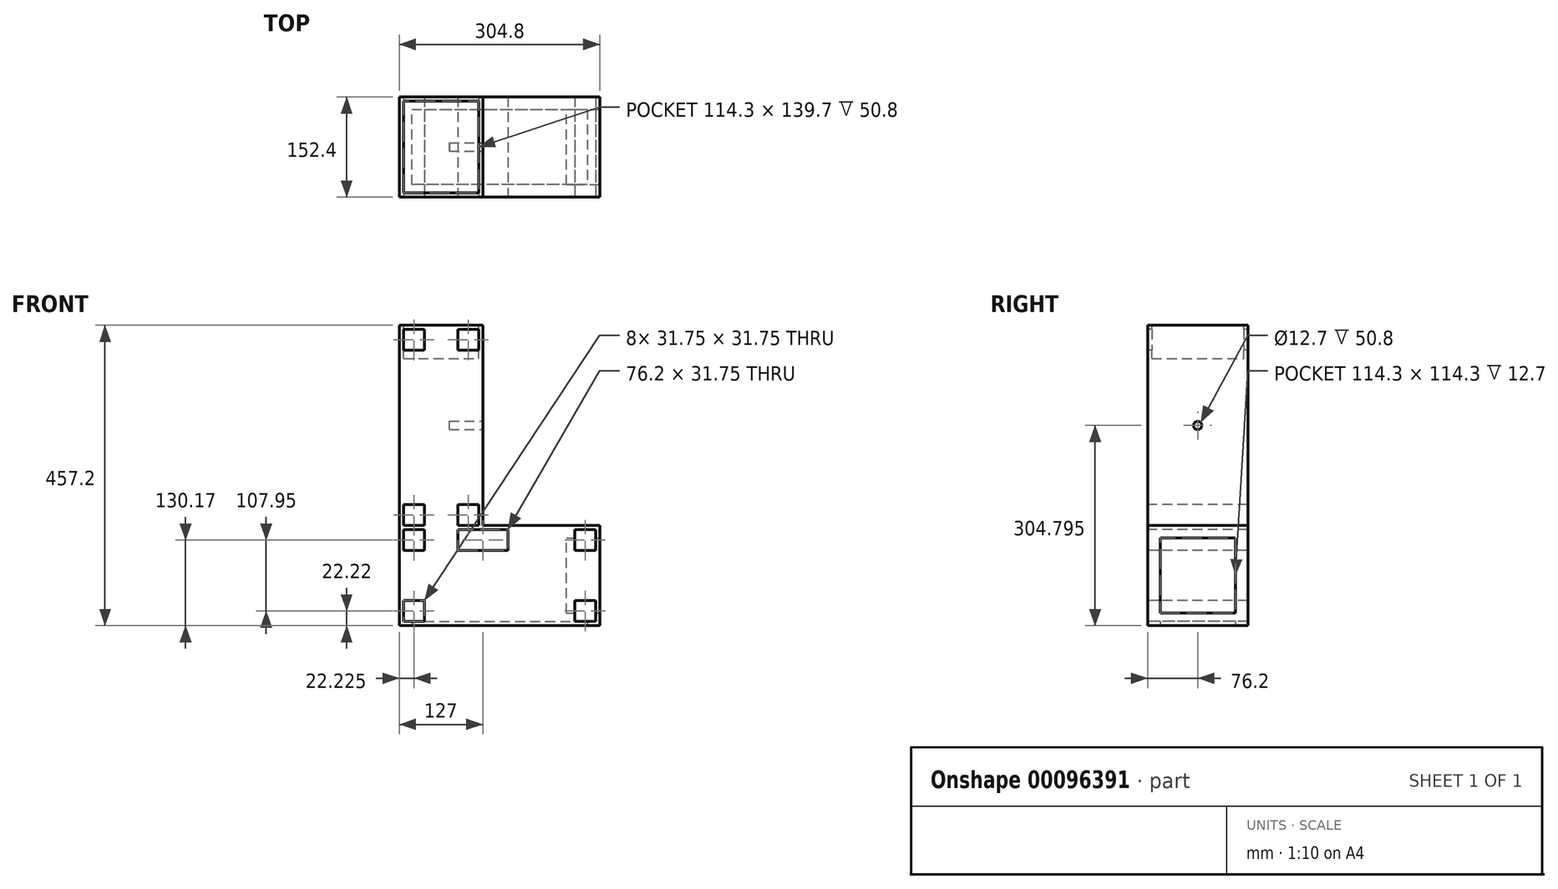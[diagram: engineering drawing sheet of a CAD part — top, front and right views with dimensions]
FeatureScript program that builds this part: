
annotation { "Feature Type Name" : "Feature", "Feature Type Description" : "" }
export const myFeature = defineFeature(function(context is Context, id is Id, definition is map)
    precondition{}
    {
        {
            var Q0;
            Q0=qCreatedBy(makeId("Front.planeOp"),FACE);
            var sketch = newSketch(context, id + "F0", { "sketchPlane" : qUnion([Q0])});
            skLineSegment(sketch, "E0", {"start": v(-127, -226.18) * mm, "end": v(177.8, -226.18) * mm});
            skLineSegment(sketch, "E1", {"start": v(177.8, -226.18) * mm, "end": v(177.8, -73.78) * mm});
            skLineSegment(sketch, "E2", {"start": v(177.8, -73.78) * mm, "end": v(0, -73.78) * mm});
            skLineSegment(sketch, "E3", {"start": v(-127, -226.18) * mm, "end": v(-127, 231.02) * mm});
            skLineSegment(sketch, "E4", {"start": v(-127, 231.02) * mm, "end": v(0, 231.02) * mm});
            skLineSegment(sketch, "E5", {"start": v(0, 231.02) * mm, "end": v(0, -73.78) * mm});
            skLineSegment(sketch, "E6", {"start": v(177.8, -226.18) * mm, "end": v(177.8, -188.08) * mm});
            skLineSegment(sketch, "E7", {"start": v(177.8, -188.08) * mm, "end": v(139.7, -188.08) * mm});
            skLineSegment(sketch, "E8", {"start": v(139.7, -188.08) * mm, "end": v(139.7, -226.18) * mm});
            skLineSegment(sketch, "E9", {"start": v(-127, -226.18) * mm, "end": v(-88.9, -226.18) * mm});
            skLineSegment(sketch, "E10", {"start": v(-88.9, -226.18) * mm, "end": v(-88.9, -188.08) * mm});
            skLineSegment(sketch, "E11", {"start": v(-88.9, -188.08) * mm, "end": v(-127, -188.08) * mm});
            skLineSegment(sketch, "E12", {"start": v(-127, 231.02) * mm, "end": v(-127, 192.92) * mm});
            skLineSegment(sketch, "E13", {"start": v(-127, 192.92) * mm, "end": v(-88.9, 192.92) * mm});
            skLineSegment(sketch, "E14", {"start": v(-88.9, 192.92) * mm, "end": v(-88.9, 231.02) * mm});
            skLineSegment(sketch, "E15", {"start": v(-38.1, 231.02) * mm, "end": v(-38.1, 192.92) * mm});
            skLineSegment(sketch, "E16", {"start": v(-38.1, 192.92) * mm, "end": v(0, 192.92) * mm});
            skLineSegment(sketch, "E17", {"start": v(0, -35.68) * mm, "end": v(-38.1, -35.68) * mm});
            skLineSegment(sketch, "E18", {"start": v(-38.1, -35.68) * mm, "end": v(-38.1, -111.88) * mm});
            skLineSegment(sketch, "E19", {"start": v(-38.1, -111.88) * mm, "end": v(38.1, -111.88) * mm});
            skLineSegment(sketch, "E20", {"start": v(38.1, -111.88) * mm, "end": v(38.1, -73.78) * mm});
            skLineSegment(sketch, "E21", {"start": v(139.7, -73.78) * mm, "end": v(139.7, -111.88) * mm});
            skLineSegment(sketch, "E22", {"start": v(139.7, -111.88) * mm, "end": v(177.8, -111.88) * mm});
            skLineSegment(sketch, "E23", {"start": v(-120.65, 192.92) * mm, "end": v(-120.65, 231.02) * mm});
            skLineSegment(sketch, "E24", {"start": v(-127, 224.67) * mm, "end": v(-88.9, 224.67) * mm});
            skLineSegment(sketch, "E25", {"start": v(0, 224.67) * mm, "end": v(-38.1, 224.67) * mm});
            skLineSegment(sketch, "E26", {"start": v(-6.35, 231.02) * mm, "end": v(-6.35, 192.92) * mm});
            skLineSegment(sketch, "E27", {"start": v(-6.35, -35.68) * mm, "end": v(-6.35, -80.13) * mm});
            skLineSegment(sketch, "E28", {"start": v(-6.35, -80.13) * mm, "end": v(38.1, -80.13) * mm});
            skLineSegment(sketch, "E29", {"start": v(139.7, -80.13) * mm, "end": v(177.8, -80.13) * mm});
            skLineSegment(sketch, "E30", {"start": v(171.45, -73.78) * mm, "end": v(171.45, -111.88) * mm});
            skLineSegment(sketch, "E31", {"start": v(171.45, -188.08) * mm, "end": v(171.45, -226.18) * mm});
            skLineSegment(sketch, "E32", {"start": v(-120.65, -188.08) * mm, "end": v(-120.65, -226.18) * mm});
            skLineSegment(sketch, "E33", {"start": v(-127, -219.83) * mm, "end": v(-88.9, -219.83) * mm});
            skLineSegment(sketch, "E34", {"start": v(139.7, -219.83) * mm, "end": v(177.8, -219.83) * mm});
            skSolve(sketch);
        }
        {
            var Q0;
            {var subQ27=sQuery(id+"F0.wireOp",EDGE,"E18");Q0=makeQuery(id+"F0.imprint","IMPRINT",FACE,{"disambiguationData":[TD([[makeQuery(id+"F0.imprint","IMPRINT",EDGE,{"derivedFrom":subQ27}),-1.0]])]});}
            var Q1;
            {var subQ0=sQuery(id+"F0.wireOp",EDGE,"E16");var subQ1=sQuery(id+"F0.wireOp",EDGE,"E5");var subQ2=makeQuery(id+"F0.imprint","INTERSECT",VERTEX,{"derivedFrom":[subQ1,subQ0]});Q1=makeQuery(id+"F0.imprint","IMPRINT",FACE,{"disambiguationData":[TD([[makeQuery(id+"F0.imprint","IMPRINT",EDGE,{"disambiguationData":[TD([[subQ2,1.0]])],"derivedFrom":subQ1}),-1.0]])]});}
            var Q2;
            {var subQ0=sQuery(id+"F0.wireOp",EDGE,"E15");var subQ1=sQuery(id+"F0.wireOp",EDGE,"E4");var subQ2=makeQuery(id+"F0.imprint","INTERSECT",VERTEX,{"derivedFrom":[subQ1,subQ0]});Q2=makeQuery(id+"F0.imprint","IMPRINT",FACE,{"disambiguationData":[TD([[makeQuery(id+"F0.imprint","IMPRINT",EDGE,{"disambiguationData":[TD([[subQ2,-1.0]])],"derivedFrom":subQ1}),-1.0]])]});}
            var Q3;
            {var subQ0=sQuery(id+"F0.wireOp",EDGE,"E16");var subQ1=sQuery(id+"F0.wireOp",EDGE,"E15");var subQ2=makeQuery(id+"F0.imprint","INTERSECT",VERTEX,{"derivedFrom":[subQ1,subQ0]});Q3=makeQuery(id+"F0.imprint","IMPRINT",FACE,{"disambiguationData":[TD([[makeQuery(id+"F0.imprint","IMPRINT",EDGE,{"disambiguationData":[TD([[subQ2,1.0]])],"derivedFrom":subQ1}),1.0]])]});}
            var Q4;
            {var subQ0=sQuery(id+"F0.wireOp",EDGE,"E5");var subQ1=sQuery(id+"F0.wireOp",EDGE,"E4");var subQ2=makeQuery(id+"F0.imprint","INTERSECT",VERTEX,{"derivedFrom":[subQ1,subQ0]});Q4=makeQuery(id+"F0.imprint","IMPRINT",FACE,{"disambiguationData":[TD([[makeQuery(id+"F0.imprint","IMPRINT",EDGE,{"disambiguationData":[TD([[subQ2,1.0]])],"derivedFrom":subQ1}),-1.0]])]});}
            var Q5;
            {var subQ0=sQuery(id+"F0.wireOp",EDGE,"E12");var subQ1=sQuery(id+"F0.wireOp",EDGE,"E4");var subQ2=makeQuery(id+"F0.imprint","INTERSECT",VERTEX,{"derivedFrom":[subQ1,subQ0]});Q5=makeQuery(id+"F0.imprint","IMPRINT",FACE,{"disambiguationData":[TD([[makeQuery(id+"F0.imprint","IMPRINT",EDGE,{"disambiguationData":[TD([[subQ2,-1.0]])],"derivedFrom":subQ1}),-1.0]])]});}
            var Q6;
            {var subQ0=sQuery(id+"F0.wireOp",EDGE,"E14");var subQ1=sQuery(id+"F0.wireOp",EDGE,"E4");var subQ2=makeQuery(id+"F0.imprint","INTERSECT",VERTEX,{"derivedFrom":[subQ1,subQ0]});Q6=makeQuery(id+"F0.imprint","IMPRINT",FACE,{"disambiguationData":[TD([[makeQuery(id+"F0.imprint","IMPRINT",EDGE,{"disambiguationData":[TD([[subQ2,1.0]])],"derivedFrom":subQ1}),-1.0]])]});}
            var Q7;
            {var subQ0=sQuery(id+"F0.wireOp",EDGE,"E14");var subQ1=sQuery(id+"F0.wireOp",EDGE,"E13");var subQ2=makeQuery(id+"F0.imprint","INTERSECT",VERTEX,{"derivedFrom":[subQ1,subQ0]});Q7=makeQuery(id+"F0.imprint","IMPRINT",FACE,{"disambiguationData":[TD([[makeQuery(id+"F0.imprint","IMPRINT",EDGE,{"disambiguationData":[TD([[subQ2,1.0]])],"derivedFrom":subQ1}),1.0]])]});}
            var Q8;
            {var subQ0=sQuery(id+"F0.wireOp",EDGE,"E13");var subQ5=sQuery(id+"F0.wireOp",EDGE,"E23");var subQ6=makeQuery(id+"F0.imprint","INTERSECT",VERTEX,{"derivedFrom":[subQ0,subQ5]});Q8=makeQuery(id+"F0.imprint","IMPRINT",FACE,{"disambiguationData":[TD([[makeQuery(id+"F0.imprint","IMPRINT",EDGE,{"disambiguationData":[TD([[subQ6,-1.0]])],"derivedFrom":subQ5}),1.0]])]});}
            var Q9;
            {var subQ3=sQuery(id+"F0.wireOp",EDGE,"E27");Q9=makeQuery(id+"F0.imprint","IMPRINT",FACE,{"disambiguationData":[TD([[makeQuery(id+"F0.imprint","IMPRINT",EDGE,{"derivedFrom":subQ3}),1.0]])]});}
            var Q10;
            {var subQ4=sQuery(id+"F0.wireOp",EDGE,"E18");Q10=makeQuery(id+"F0.imprint","IMPRINT",FACE,{"disambiguationData":[TD([[makeQuery(id+"F0.imprint","IMPRINT",EDGE,{"derivedFrom":subQ4}),1.0]])]});}
            var Q11;
            {var subQ0=sQuery(id+"F0.wireOp",EDGE,"E22");var subQ1=sQuery(id+"F0.wireOp",EDGE,"E21");var subQ2=makeQuery(id+"F0.imprint","INTERSECT",VERTEX,{"derivedFrom":[subQ1,subQ0]});Q11=makeQuery(id+"F0.imprint","IMPRINT",FACE,{"disambiguationData":[TD([[makeQuery(id+"F0.imprint","IMPRINT",EDGE,{"disambiguationData":[TD([[subQ2,1.0]])],"derivedFrom":subQ1}),1.0]])]});}
            var Q12;
            {var subQ0=sQuery(id+"F0.wireOp",EDGE,"E21");var subQ1=sQuery(id+"F0.wireOp",EDGE,"E2");var subQ2=makeQuery(id+"F0.imprint","INTERSECT",VERTEX,{"derivedFrom":[subQ1,subQ0]});Q12=makeQuery(id+"F0.imprint","IMPRINT",FACE,{"disambiguationData":[TD([[makeQuery(id+"F0.imprint","IMPRINT",EDGE,{"disambiguationData":[TD([[subQ2,1.0]])],"derivedFrom":subQ1}),1.0]])]});}
            var Q13;
            {var subQ0=sQuery(id+"F0.wireOp",EDGE,"E2");var subQ1=sQuery(id+"F0.wireOp",EDGE,"E1");var subQ2=makeQuery(id+"F0.imprint","INTERSECT",VERTEX,{"derivedFrom":[subQ1,subQ0]});Q13=makeQuery(id+"F0.imprint","IMPRINT",FACE,{"disambiguationData":[TD([[makeQuery(id+"F0.imprint","IMPRINT",EDGE,{"disambiguationData":[TD([[subQ2,1.0]])],"derivedFrom":subQ1}),1.0]])]});}
            var Q14;
            {var subQ0=sQuery(id+"F0.wireOp",EDGE,"E22");var subQ1=sQuery(id+"F0.wireOp",EDGE,"E1");var subQ2=makeQuery(id+"F0.imprint","INTERSECT",VERTEX,{"derivedFrom":[subQ1,subQ0]});Q14=makeQuery(id+"F0.imprint","IMPRINT",FACE,{"disambiguationData":[TD([[makeQuery(id+"F0.imprint","IMPRINT",EDGE,{"disambiguationData":[TD([[subQ2,-1.0]])],"derivedFrom":subQ1}),1.0]])]});}
            var Q15;
            {var subQ0=sQuery(id+"F0.wireOp",EDGE,"E6");var subQ1=sQuery(id+"F0.wireOp",EDGE,"E0");var subQ2=makeQuery(id+"F0.imprint","INTERSECT",VERTEX,{"derivedFrom":[subQ1,subQ0]});Q15=makeQuery(id+"F0.imprint","IMPRINT",FACE,{"disambiguationData":[TD([[makeQuery(id+"F0.imprint","IMPRINT",EDGE,{"disambiguationData":[TD([[subQ2,1.0]])],"derivedFrom":subQ1}),1.0]])]});}
            var Q16;
            {var subQ0=sQuery(id+"F0.wireOp",EDGE,"E8");var subQ1=sQuery(id+"F0.wireOp",EDGE,"E0");var subQ2=makeQuery(id+"F0.imprint","INTERSECT",VERTEX,{"derivedFrom":[subQ1,subQ0]});Q16=makeQuery(id+"F0.imprint","IMPRINT",FACE,{"disambiguationData":[TD([[makeQuery(id+"F0.imprint","IMPRINT",EDGE,{"disambiguationData":[TD([[subQ2,-1.0]])],"derivedFrom":subQ1}),1.0]])]});}
            var Q17;
            {var subQ0=sQuery(id+"F0.wireOp",EDGE,"E8");var subQ1=sQuery(id+"F0.wireOp",EDGE,"E7");var subQ2=makeQuery(id+"F0.imprint","INTERSECT",VERTEX,{"derivedFrom":[subQ1,subQ0]});Q17=makeQuery(id+"F0.imprint","IMPRINT",FACE,{"disambiguationData":[TD([[makeQuery(id+"F0.imprint","IMPRINT",EDGE,{"disambiguationData":[TD([[subQ2,1.0]])],"derivedFrom":subQ1}),1.0]])]});}
            var Q18;
            {var subQ0=sQuery(id+"F0.wireOp",EDGE,"E7");var subQ5=sQuery(id+"F0.wireOp",EDGE,"E31");var subQ6=makeQuery(id+"F0.imprint","INTERSECT",VERTEX,{"derivedFrom":[subQ0,subQ5]});Q18=makeQuery(id+"F0.imprint","IMPRINT",FACE,{"disambiguationData":[TD([[makeQuery(id+"F0.imprint","IMPRINT",EDGE,{"disambiguationData":[TD([[subQ6,-1.0]])],"derivedFrom":subQ5}),1.0]])]});}
            var Q19;
            {var subQ0=sQuery(id+"F0.wireOp",EDGE,"E11");var subQ1=sQuery(id+"F0.wireOp",EDGE,"E10");var subQ2=makeQuery(id+"F0.imprint","INTERSECT",VERTEX,{"derivedFrom":[subQ1,subQ0]});Q19=makeQuery(id+"F0.imprint","IMPRINT",FACE,{"disambiguationData":[TD([[makeQuery(id+"F0.imprint","IMPRINT",EDGE,{"disambiguationData":[TD([[subQ2,1.0]])],"derivedFrom":subQ1}),1.0]])]});}
            var Q20;
            {var subQ0=sQuery(id+"F0.wireOp",EDGE,"E11");var subQ1=sQuery(id+"F0.wireOp",EDGE,"E3");var subQ2=makeQuery(id+"F0.imprint","INTERSECT",VERTEX,{"derivedFrom":[subQ1,subQ0]});Q20=makeQuery(id+"F0.imprint","IMPRINT",FACE,{"disambiguationData":[TD([[makeQuery(id+"F0.imprint","IMPRINT",EDGE,{"disambiguationData":[TD([[subQ2,1.0]])],"derivedFrom":subQ1}),-1.0]])]});}
            var Q21;
            {var subQ0=sQuery(id+"F0.wireOp",EDGE,"E9");var subQ1=sQuery(id+"F0.wireOp",EDGE,"E3");var subQ2=makeQuery(id+"F0.imprint","INTERSECT",VERTEX,{"derivedFrom":[subQ1,subQ0]});Q21=makeQuery(id+"F0.imprint","IMPRINT",FACE,{"disambiguationData":[TD([[makeQuery(id+"F0.imprint","IMPRINT",EDGE,{"disambiguationData":[TD([[subQ2,-1.0]])],"derivedFrom":subQ1}),-1.0]])]});}
            var Q22;
            {var subQ1=sQuery(id+"F0.wireOp",EDGE,"E9");var subQ3=sQuery(id+"F0.wireOp",EDGE,"E32");var subQ4=makeQuery(id+"F0.imprint","INTERSECT",VERTEX,{"derivedFrom":[subQ1,subQ3]});Q22=makeQuery(id+"F0.imprint","IMPRINT",FACE,{"disambiguationData":[TD([[makeQuery(id+"F0.imprint","IMPRINT",EDGE,{"disambiguationData":[TD([[subQ4,1.0]])],"derivedFrom":subQ3}),1.0]])]});}
            extrude(context, id + "F1", {"entities" : qUnion([Q0, Q1, Q2, Q3, Q4, Q5, Q6, Q7, Q8, Q9, Q10, Q11, Q12, Q13, Q14, Q15, Q16, Q17, Q18, Q19, Q20, Q21, Q22]), "endBound" : BoundingType.SYMMETRIC, "depth" : 152.4 * mm});
        }
        {
            var Q0;
            Q0=makeQuery(id+"F1.opExtrude","CAP_FACE",FACE,{"disambiguationData":[OSD([sQuery(id+"F0.wireOp",EDGE,"E0"),sQuery(id+"F0.wireOp",EDGE,"E1"),sQuery(id+"F0.wireOp",EDGE,"E2"),sQuery(id+"F0.wireOp",EDGE,"E3"),sQuery(id+"F0.wireOp",EDGE,"E4"),sQuery(id+"F0.wireOp",EDGE,"E5"),sQuery(id+"F0.wireOp",EDGE,"E6"),sQuery(id+"F0.wireOp",EDGE,"E9"),sQuery(id+"F0.wireOp",EDGE,"E12")])],"isStart":false});
            var sketch = newSketch(context, id + "F2", { "sketchPlane" : qUnion([Q0])});
            skLineSegment(sketch, "E35.0", {"start": v(-127, 192.92) * mm, "end": v(-88.9, 192.92) * mm});
            skLineSegment(sketch, "E35.1", {"start": v(-88.9, 192.92) * mm, "end": v(-88.9, 231.02) * mm});
            skLineSegment(sketch, "E35.2", {"start": v(-127, 224.67) * mm, "end": v(-88.9, 224.67) * mm});
            skLineSegment(sketch, "E35.3", {"start": v(-120.65, 192.92) * mm, "end": v(-120.65, 231.02) * mm});
            skLineSegment(sketch, "E35.4", {"start": v(-38.1, 192.92) * mm, "end": v(0, 192.92) * mm});
            skLineSegment(sketch, "E35.5", {"start": v(-38.1, 231.02) * mm, "end": v(-38.1, 192.92) * mm});
            skLineSegment(sketch, "E35.6", {"start": v(-6.35, 231.02) * mm, "end": v(-6.35, 192.92) * mm});
            skLineSegment(sketch, "E35.7", {"start": v(0, 224.67) * mm, "end": v(-38.1, 224.67) * mm});
            skLineSegment(sketch, "E35.11", {"start": v(-6.35, -80.13) * mm, "end": v(38.1, -80.13) * mm});
            skLineSegment(sketch, "E35.12", {"start": v(-38.1, -111.88) * mm, "end": v(38.1, -111.88) * mm});
            skLineSegment(sketch, "E35.13", {"start": v(38.1, -111.88) * mm, "end": v(38.1, -73.78) * mm});
            skLineSegment(sketch, "E35.14", {"start": v(139.7, -73.78) * mm, "end": v(139.7, -111.88) * mm});
            skLineSegment(sketch, "E35.15", {"start": v(139.7, -111.88) * mm, "end": v(177.8, -111.88) * mm});
            skLineSegment(sketch, "E35.16", {"start": v(171.45, -73.78) * mm, "end": v(171.45, -111.88) * mm});
            skLineSegment(sketch, "E35.17", {"start": v(139.7, -80.13) * mm, "end": v(177.8, -80.13) * mm});
            skLineSegment(sketch, "E35.18", {"start": v(177.8, -188.08) * mm, "end": v(139.7, -188.08) * mm});
            skLineSegment(sketch, "E35.19", {"start": v(171.45, -188.08) * mm, "end": v(171.45, -226.18) * mm});
            skLineSegment(sketch, "E35.20", {"start": v(139.7, -219.83) * mm, "end": v(177.8, -219.83) * mm});
            skLineSegment(sketch, "E35.21", {"start": v(139.7, -188.08) * mm, "end": v(139.7, -226.18) * mm});
            skLineSegment(sketch, "E35.22", {"start": v(-88.9, -226.18) * mm, "end": v(-88.9, -188.08) * mm});
            skLineSegment(sketch, "E35.23", {"start": v(-88.9, -188.08) * mm, "end": v(-127, -188.08) * mm});
            skLineSegment(sketch, "E35.24", {"start": v(-120.65, -188.08) * mm, "end": v(-120.65, -226.18) * mm});
            skLineSegment(sketch, "E35.25", {"start": v(-127, -219.83) * mm, "end": v(-88.9, -219.83) * mm});
            skLineSegment(sketch, "E36", {"start": v(-88.9, -73.78) * mm, "end": v(-120.65, -73.78) * mm});
            skLineSegment(sketch, "E37", {"start": v(-88.9, -80.13) * mm, "end": v(-120.65, -80.13) * mm});
            skLineSegment(sketch, "E38", {"start": v(-120.65, -111.88) * mm, "end": v(-88.9, -111.88) * mm});
            skLineSegment(sketch, "E39", {"start": v(-120.65, -111.88) * mm, "end": v(-120.65, -73.78) * mm});
            skLineSegment(sketch, "E40", {"start": v(-88.9, -111.88) * mm, "end": v(-88.9, -73.78) * mm});
            skLineSegment(sketch, "E41", {"start": v(-88.9, -73.78) * mm, "end": v(-88.9, -42.03) * mm});
            skLineSegment(sketch, "E42", {"start": v(-120.65, -73.78) * mm, "end": v(-120.65, -42.03) * mm});
            skLineSegment(sketch, "E43", {"start": v(-120.65, -42.03) * mm, "end": v(-88.9, -42.03) * mm});
            skLineSegment(sketch, "E44", {"start": v(0, -73.78) * mm, "end": v(-38.1, -73.78) * mm});
            skLineSegment(sketch, "E45", {"start": v(-38.1, -111.88) * mm, "end": v(-38.1, -73.78) * mm});
            skLineSegment(sketch, "E46", {"start": v(-6.35, -80.13) * mm, "end": v(-6.35, -73.78) * mm});
            skLineSegment(sketch, "E47", {"start": v(-6.35, -73.78) * mm, "end": v(-6.35, -42.03) * mm});
            skLineSegment(sketch, "E48", {"start": v(-38.1, -73.78) * mm, "end": v(-38.1, -42.03) * mm});
            skLineSegment(sketch, "E49", {"start": v(-38.1, -42.03) * mm, "end": v(-6.35, -42.03) * mm});
            skLineSegment(sketch, "E50", {"start": v(-6.35, -80.13) * mm, "end": v(-38.1, -80.13) * mm});
            skSolve(sketch);
        }
        {
            var Q0;
            {var subQ0=sQuery(id+"F2.wireOp",EDGE,"E35.1");var subQ1=sQuery(id+"F2.wireOp",EDGE,"E35.0");var subQ2=makeQuery(id+"F2.imprint","INTERSECT",VERTEX,{"derivedFrom":[subQ1,subQ0]});Q0=makeQuery(id+"F2.imprint","IMPRINT",FACE,{"disambiguationData":[TD([[makeQuery(id+"F2.imprint","IMPRINT",EDGE,{"disambiguationData":[TD([[subQ2,1.0]])],"derivedFrom":subQ1}),1.0]])]});}
            var Q1;
            {var subQ0=sQuery(id+"F2.wireOp",EDGE,"E35.5");var subQ1=sQuery(id+"F2.wireOp",EDGE,"E35.4");var subQ2=makeQuery(id+"F2.imprint","INTERSECT",VERTEX,{"derivedFrom":[subQ1,subQ0]});Q1=makeQuery(id+"F2.imprint","IMPRINT",FACE,{"disambiguationData":[TD([[makeQuery(id+"F2.imprint","IMPRINT",EDGE,{"disambiguationData":[TD([[subQ2,-1.0]])],"derivedFrom":subQ1}),1.0]])]});}
            var Q2;
            {var subQ1=sQuery(id+"F2.wireOp",EDGE,"E35.9");Q2=makeQuery(id+"F2.imprint","IMPRINT",FACE,{"disambiguationData":[TD([[makeQuery(id+"F2.imprint","IMPRINT",EDGE,{"derivedFrom":subQ1}),1.0]])]});}
            var Q3;
            {var subQ0=sQuery(id+"F2.wireOp",EDGE,"E35.23");var subQ1=sQuery(id+"F2.wireOp",EDGE,"E35.22");var subQ2=makeQuery(id+"F2.imprint","INTERSECT",VERTEX,{"derivedFrom":[subQ1,subQ0]});Q3=makeQuery(id+"F2.imprint","IMPRINT",FACE,{"disambiguationData":[TD([[makeQuery(id+"F2.imprint","IMPRINT",EDGE,{"disambiguationData":[TD([[subQ2,1.0]])],"derivedFrom":subQ1}),1.0]])]});}
            var Q4;
            {var subQ0=sQuery(id+"F2.wireOp",EDGE,"E35.15");var subQ1=sQuery(id+"F2.wireOp",EDGE,"E35.14");var subQ2=makeQuery(id+"F2.imprint","INTERSECT",VERTEX,{"derivedFrom":[subQ1,subQ0]});Q4=makeQuery(id+"F2.imprint","IMPRINT",FACE,{"disambiguationData":[TD([[makeQuery(id+"F2.imprint","IMPRINT",EDGE,{"disambiguationData":[TD([[subQ2,1.0]])],"derivedFrom":subQ1}),1.0]])]});}
            var Q5;
            {var subQ0=sQuery(id+"F2.wireOp",EDGE,"E35.21");var subQ1=sQuery(id+"F2.wireOp",EDGE,"E35.18");var subQ2=makeQuery(id+"F2.imprint","INTERSECT",VERTEX,{"derivedFrom":[subQ1,subQ0]});Q5=makeQuery(id+"F2.imprint","IMPRINT",FACE,{"disambiguationData":[TD([[makeQuery(id+"F2.imprint","IMPRINT",EDGE,{"disambiguationData":[TD([[subQ2,1.0]])],"derivedFrom":subQ1}),1.0]])]});}
            extrude(context, id + "F3", {"entities" : qUnion([Q0, Q1, Q2, Q3, Q4, Q5]), "operationType" : NewBodyOperationType.REMOVE, "oppositeDirection" : true, "depth" : 177.8 * mm});
        }
        {
            var Q0;
            Q0=makeQuery(id+"F1.opExtrude","SWEPT_FACE",FACE,{"disambiguationData":[OSD([sQuery(id+"F0.wireOp",EDGE,"E1"),sQuery(id+"F0.wireOp",EDGE,"E6")])]});
            var sketch = newSketch(context, id + "F4", { "sketchPlane" : qUnion([Q0])});
            skLineSegment(sketch, "E51.0", {"start": v(-57.15, -207.13) * mm, "end": v(-57.15, -92.83) * mm});
            skLineSegment(sketch, "E51.1", {"start": v(-57.15, -207.13) * mm, "end": v(57.15, -207.13) * mm});
            skLineSegment(sketch, "E51.2", {"start": v(57.15, -207.13) * mm, "end": v(57.15, -92.83) * mm});
            skLineSegment(sketch, "E51.3", {"start": v(-57.15, -92.83) * mm, "end": v(57.15, -92.83) * mm});
            skSolve(sketch);
        }
        {
            var Q0;
            Q0 = qSketchRegion(id + "F4", true);
            extrude(context, id + "F5", {"entities" : qUnion([Q0]), "operationType" : NewBodyOperationType.REMOVE, "oppositeDirection" : true, "depth" : 50.8 * mm});
        }
        {
            var Q0;
            Q0=makeQuery(id+"F1.opExtrude","SWEPT_FACE",FACE,{"disambiguationData":[OSD([sQuery(id+"F0.wireOp",EDGE,"E4")])]});
            var sketch = newSketch(context, id + "F6", { "sketchPlane" : qUnion([Q0])});
            skLineSegment(sketch, "E52.0", {"start": v(-120.65, -69.85) * mm, "end": v(-6.35, -69.85) * mm});
            skLineSegment(sketch, "E52.1", {"start": v(-120.65, -69.85) * mm, "end": v(-120.65, 69.85) * mm});
            skLineSegment(sketch, "E52.2", {"start": v(-120.65, 69.85) * mm, "end": v(-6.35, 69.85) * mm});
            skLineSegment(sketch, "E52.3", {"start": v(-6.35, -69.85) * mm, "end": v(-6.35, 69.85) * mm});
            skSolve(sketch);
        }
        {
            var Q0;
            Q0=makeQuery(id+"F6.imprint","IMPRINT",FACE,{"disambiguationData":[TD([[makeQuery(id+"F6.imprint","IMPRINT",EDGE,{"derivedFrom":sQuery(id+"F6.wireOp",EDGE,"E52.0")}),1.0]])]});
            extrude(context, id + "F7", {"entities" : qUnion([Q0]), "operationType" : NewBodyOperationType.REMOVE, "oppositeDirection" : true, "depth" : 50.8 * mm});
        }
        {
            var Q0;
            Q0=makeQuery(id+"F1.opExtrude","SWEPT_FACE",FACE,{"disambiguationData":[OSD([sQuery(id+"F0.wireOp",EDGE,"E5")])]});
            var sketch = newSketch(context, id + "F8", { "sketchPlane" : qUnion([Q0])});
            skLineSegment(sketch, "E53", {"start": v(0, 231.02) * mm, "end": v(0, 78.62) * mm});
            skPoint(sketch, "E53.endSnap0", {"position": v(0, -73.78) * mm});
            skCircle(sketch, "E54", {"center": v(0, 78.62) * mm, "radius": 6.35 * mm});
            skSolve(sketch);
        }
        {
            var Q0;
            Q0=makeQuery(id+"F8.imprint","IMPRINT",FACE,{"disambiguationData":[TD([[makeQuery(id+"F8.imprint","IMPRINT",EDGE,{"derivedFrom":sQuery(id+"F8.wireOp",EDGE,"E54")}),1.0]])]});
            extrude(context, id + "F9", {"entities" : qUnion([Q0]), "operationType" : NewBodyOperationType.REMOVE, "oppositeDirection" : true, "depth" : 50.8 * mm});
        }
        {
            var Q0;
            Q0=makeQuery(id+"F1.opExtrude","SWEPT_FACE",FACE,{"disambiguationData":[OSD([sQuery(id+"F0.wireOp",EDGE,"E2")])]});
            var sketch = newSketch(context, id + "F10", { "sketchPlane" : qUnion([Q0])});
            skLineSegment(sketch, "E55", {"start": v(0, 76.2) * mm, "end": v(-127, 76.2) * mm});
            skLineSegment(sketch, "E56", {"start": v(-127, 76.2) * mm, "end": v(-127, -76.2) * mm});
            skLineSegment(sketch, "E57", {"start": v(-127, -76.2) * mm, "end": v(0, -76.2) * mm});
            skLineSegment(sketch, "E58", {"start": v(0, 0) * mm, "end": v(-63.5, 0) * mm});
            skCircle(sketch, "E59", {"center": v(-63.5, 0) * mm, "radius": 19.05 * mm});
            skSolve(sketch);
        }
        {
            var Q0;
            {var subQ4=sQuery(id+"F10.wireOp",EDGE,"E55");Q0=makeQuery(id+"F10.imprint","IMPRINT",FACE,{"disambiguationData":[TD([[makeQuery(id+"F10.imprint","IMPRINT",EDGE,{"derivedFrom":subQ4}),1.0]])]});}
            extrude(context, id + "F11", {"entities" : qUnion([Q0]), "operationType" : NewBodyOperationType.ADD, "oppositeDirection" : true, "depth" : 6.35 * mm});
        }
        {
            var Q0;
            {var subQ5=sQuery(id+"F2.wireOp",EDGE,"E36");Q0=makeQuery(id+"F2.imprint","IMPRINT",FACE,{"disambiguationData":[TD([[makeQuery(id+"F2.imprint","IMPRINT",EDGE,{"derivedFrom":subQ5}),-1.0]])]});}
            var Q1;
            {var subQ3=sQuery(id+"F2.wireOp",EDGE,"E37");Q1=makeQuery(id+"F2.imprint","IMPRINT",FACE,{"disambiguationData":[TD([[makeQuery(id+"F2.imprint","IMPRINT",EDGE,{"derivedFrom":subQ3}),1.0]])]});}
            var Q2;
            {var subQ2=sQuery(id+"F2.wireOp",EDGE,"E47");Q2=makeQuery(id+"F2.imprint","IMPRINT",FACE,{"disambiguationData":[TD([[makeQuery(id+"F2.imprint","IMPRINT",EDGE,{"derivedFrom":subQ2}),1.0]])]});}
            var Q3;
            {var subQ4=sQuery(id+"F2.wireOp",EDGE,"E35.11");Q3=makeQuery(id+"F2.imprint","IMPRINT",FACE,{"disambiguationData":[TD([[makeQuery(id+"F2.imprint","IMPRINT",EDGE,{"derivedFrom":subQ4}),-1.0]])]});}
            extrude(context, id + "F12", {"entities" : qUnion([Q0, Q1, Q2, Q3]), "operationType" : NewBodyOperationType.REMOVE, "oppositeDirection" : true, "depth" : 152.4 * mm});
        }
        {
            var Q0;
            Q0=makeQuery(id+"F1.opExtrude","SWEPT_FACE",FACE,{"disambiguationData":[OSD([sQuery(id+"F0.wireOp",EDGE,"E0"),sQuery(id+"F0.wireOp",EDGE,"E9")])]});
            var sketch = newSketch(context, id + "F13", { "sketchPlane" : qUnion([Q0])});
            skLineSegment(sketch, "E60.0", {"start": v(-107.95, -57.15) * mm, "end": v(158.75, -57.15) * mm});
            skLineSegment(sketch, "E60.1", {"start": v(-107.95, 57.15) * mm, "end": v(-107.95, -57.15) * mm});
            skLineSegment(sketch, "E60.2", {"start": v(158.75, 57.15) * mm, "end": v(-107.95, 57.15) * mm});
            skLineSegment(sketch, "E60.3", {"start": v(158.75, -57.15) * mm, "end": v(158.75, 57.15) * mm});
            skSolve(sketch);
        }
        {
            var Q0;
            Q0=makeQuery(id+"F13.imprint","IMPRINT",FACE,{"disambiguationData":[TD([[makeQuery(id+"F13.imprint","IMPRINT",EDGE,{"derivedFrom":sQuery(id+"F13.wireOp",EDGE,"E60.0")}),1.0]])]});
            extrude(context, id + "F14", {"entities" : qUnion([Q0]), "operationType" : NewBodyOperationType.REMOVE, "oppositeDirection" : true, "depth" : 6.35 * mm});
        }
    });
